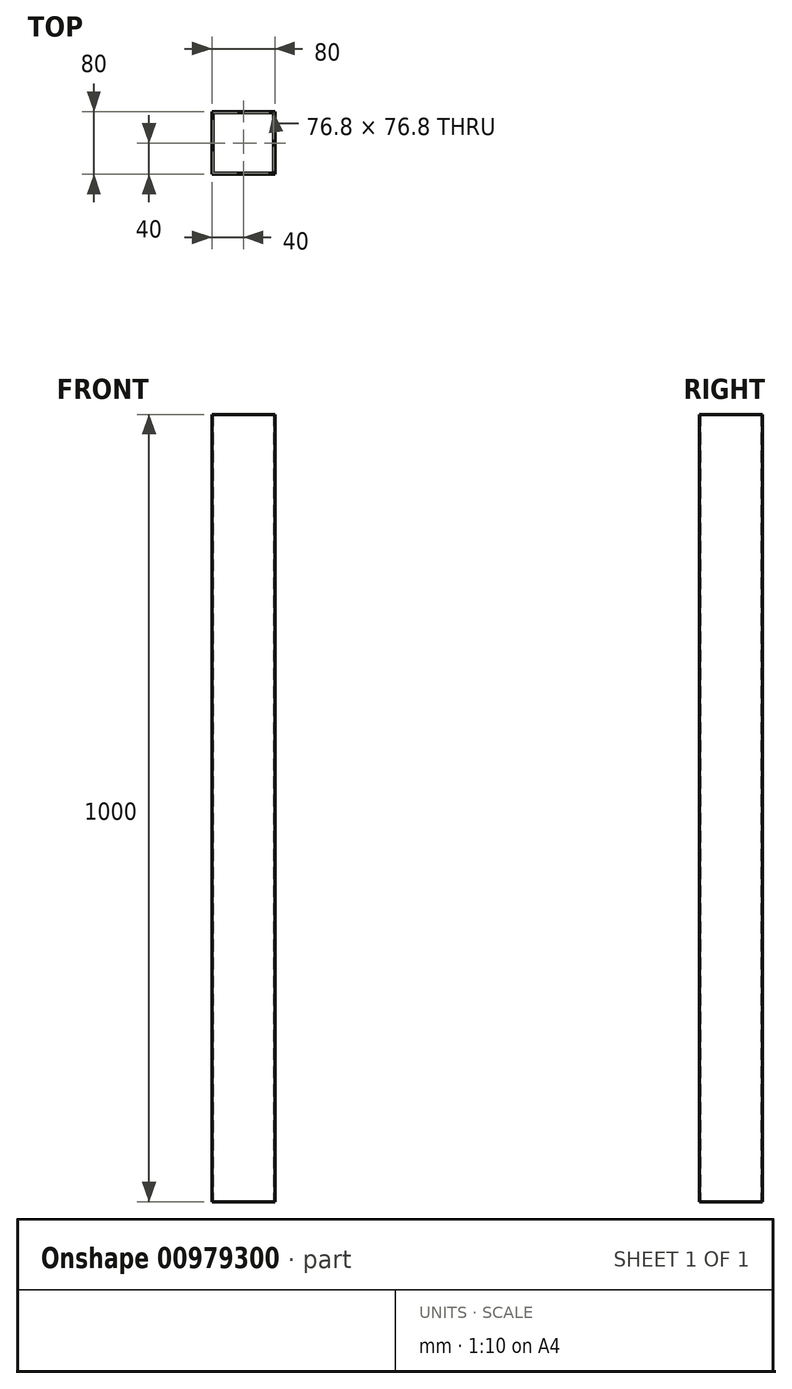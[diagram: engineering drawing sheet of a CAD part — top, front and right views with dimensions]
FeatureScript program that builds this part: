
annotation { "Feature Type Name" : "Feature", "Feature Type Description" : "" }
export const myFeature = defineFeature(function(context is Context, id is Id, definition is map)
    precondition{}
    {
        {
            var Q0;
            Q0=qCreatedBy(makeId("Top.planeOp"),FACE);
            var sketch = newSketch(context, id + "F0", { "sketchPlane" : qUnion([Q0])});
            skLineSegment(sketch, "E0.bottom", {"start": v(-40, 40) * mm, "end": v(40, 40) * mm});
            skLineSegment(sketch, "E0.top", {"start": v(-40, -40) * mm, "end": v(40, -40) * mm});
            skLineSegment(sketch, "E0.left", {"start": v(-40, 40) * mm, "end": v(-40, -40) * mm});
            skLineSegment(sketch, "E0.right", {"start": v(40, 40) * mm, "end": v(40, -40) * mm});
            skPoint(sketch, "E0.middle", {"position": v(0, 0) * mm});
            skLineSegment(sketch, "E1.bottom", {"start": v(-38.4, 38.4) * mm, "end": v(38.4, 38.4) * mm});
            skLineSegment(sketch, "E1.top", {"start": v(-38.4, -38.4) * mm, "end": v(38.4, -38.4) * mm});
            skLineSegment(sketch, "E1.left", {"start": v(-38.4, 38.4) * mm, "end": v(-38.4, -38.4) * mm});
            skLineSegment(sketch, "E1.right", {"start": v(38.4, 38.4) * mm, "end": v(38.4, -38.4) * mm});
            skSolve(sketch);
        }
        {
            var Q0;
            Q0=makeQuery(id+"F0.imprint","IMPRINT",FACE,{"disambiguationData":[TD([[makeQuery(id+"F0.imprint","IMPRINT",EDGE,{"derivedFrom":sQuery(id+"F0.wireOp",EDGE,"E0.bottom")}),-1.0]])]});
            extrude(context, id + "F1", {"entities" : qUnion([Q0]), "depth" : 1000 * mm, "offsetDistance" : 25 * mm});
        }
    });
